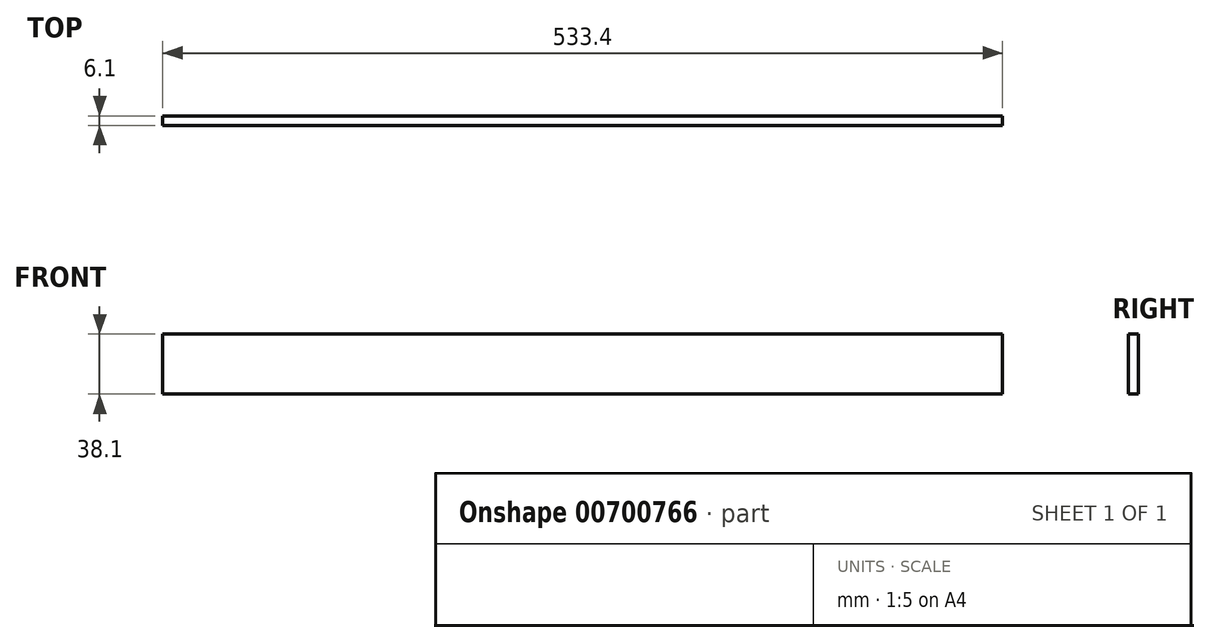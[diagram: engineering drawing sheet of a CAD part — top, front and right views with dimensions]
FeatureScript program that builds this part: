
annotation { "Feature Type Name" : "Feature", "Feature Type Description" : "" }
export const myFeature = defineFeature(function(context is Context, id is Id, definition is map)
    precondition{}
    {
        {
            var Q0;
            Q0=qCreatedBy(makeId("Front.planeOp"),FACE);
            var sketch = newSketch(context, id + "F0", { "sketchPlane" : qUnion([Q0])});
            skLineSegment(sketch, "E0.bottom", {"start": v(-266.7, 19.05) * mm, "end": v(266.7, 19.05) * mm});
            skLineSegment(sketch, "E0.top", {"start": v(-266.7, -19.05) * mm, "end": v(266.7, -19.05) * mm});
            skLineSegment(sketch, "E0.left", {"start": v(-266.7, 19.05) * mm, "end": v(-266.7, -19.05) * mm});
            skLineSegment(sketch, "E0.right", {"start": v(266.7, 19.05) * mm, "end": v(266.7, -19.05) * mm});
            skLineSegment(sketch, "E1", {"start": v(0, 0) * mm, "end": v(12.7, 0) * mm});
            skLineSegment(sketch, "E2", {"start": v(12.7, 0) * mm, "end": v(0, 0) * mm, "construction": true});
            skLineSegment(sketch, "E3", {"start": v(0, 0) * mm, "end": v(0, 12.7) * mm, "construction": true});
            skSolve(sketch);
        }
        {
            var Q0;
            Q0=makeQuery(id+"F0.imprint","IMPRINT",FACE,{"disambiguationData":[TD([[makeQuery(id+"F0.imprint","IMPRINT",EDGE,{"derivedFrom":sQuery(id+"F0.wireOp",EDGE,"E0.bottom")}),-1.0]])]});
            extrude(context, id + "F1", {"entities" : qUnion([Q0]), "endBound" : BoundingType.SYMMETRIC, "depth" : 6.1 * mm, "offsetDistance" : 25.4 * mm});
        }
    });
